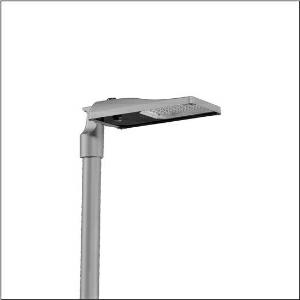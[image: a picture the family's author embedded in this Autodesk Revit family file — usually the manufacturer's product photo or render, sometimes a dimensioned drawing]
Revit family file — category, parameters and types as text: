
# Revit family: streetlight_sl_31_mini___stw1_0a_5xh6e31t08ja_04bd
name_source: partatom
category: Lighting Fixtures
units: mm (PartAtom-declared; Revit-internal decimal feet)

## family parameters
Cut with Voids When Loaded = No
Host = Face
Light Source = No
Part Type = Normal
Room Calculation Point = No
Round Connector Dimension = Use Diameter
Shared = No

## types (1)
- --- (1 x LED, 12270 lm, 82.5 W, 3000K)
    Apparent Load = 83 VA
    CIE Flux Codes = 39 75 98 100 100
    Color Rendering = 70
    Color Temperature = 3000K
    Default Elevation = 1800 mm
    Description = Streetlight SL 31 mini D4i, Desk-Remote mast luminaire for post-top, side-entry; light control with lens of PMMA; light distribution: STW1.0a, direct asymmetric distribution, for standard-compliant lighting for roads and squares; LED: luminous flux: 12.270lm, light colour: 730, colour temperature: 3000K; luminous efficacy: 148,7lm/W; control: pre-setting: logarithmic dimming characteristic, flexible luminous flux parameterisation, time-dependent luminous flux control, constant luminous flux control, power reduction, intelligent temperature release in ECG and LED module, overheat protection; luminaire housing, of diecast aluminium, SITECO metallic grey (DB 702S), corrosivity category C5 high according to DIN EN ISO 12944; cover of toughened safety glass, transparent, opened without tools; mast flange of diecast aluminium, SITECO metallic grey (DB 702S), spigot size: 76/60mm, mast flange included unmounted; cable length: 10,5m, connection cable pre-assembled; mains connection: 220..240V, AC, 50/60Hz; power consumption (at start of service life): 82,5W / (at end of service life): 90,1W / (with reduced operation 50%): 36,8W; protection rating (complete): IP66; insulation class (complete): insulation class II (safety insulation); impact resistance: IK09; certification: CE, ENEC, ENEC+, VDE, UKCA, ZD4i; permissible operating ambient temperature for outdoor applications: -40..+50°C; packaging unit: 1 piece

Light Distribution: STW1.0a
    Height = 76 mm
    Lamp = 1 x LED
    Lamp Light Flux = 12270 lm
    Lamp Power = 82.5 W
    Lamp count = 1
    Length = 547 mm
    Luminous efficacy = 149 lm/W
    Manufacturer = Siteco
    ModVariant = No
    Model = 5XH6E31T08JA
    Number of Poles = 1
    OnlyDefault = Yes
    Power Factor = 1
    Product Name = Streetlight SL 31 mini | STW1.0a
    Product group = mast luminaire | pylon top
    ProductGroupID = 6100
    Protection Class = Protection class II
    Protection Degree = IP 66
    RLX_Detail_Level = 1
    RLX_Emergency_Light_Flux = 0 lm
    RLX_Emergency_Type = 0
    RLX_Emergency_Type_DB = No
    RlxData = <blob elided: 39877 chars, md5=16b6e11f>
    Socket = socket
    Standby Power = 0 W
    System Light Flux = 12270 lm
    System Power = 83 W
    Type Comments = factory setting: luminous flux: 100 % | dim-lin: 254 | 870 mA
    Type Image = l_1300332.jpg
    URL = http://relux.com
    VarID = @adj_056755
    Voltage = 0 V
    Weight = 0.00 kg
    Width = 265 mm

## geometry (parser evidence)
native form markers: Blend x4, Sweep x10
no freeform markers — native parametric forms only
